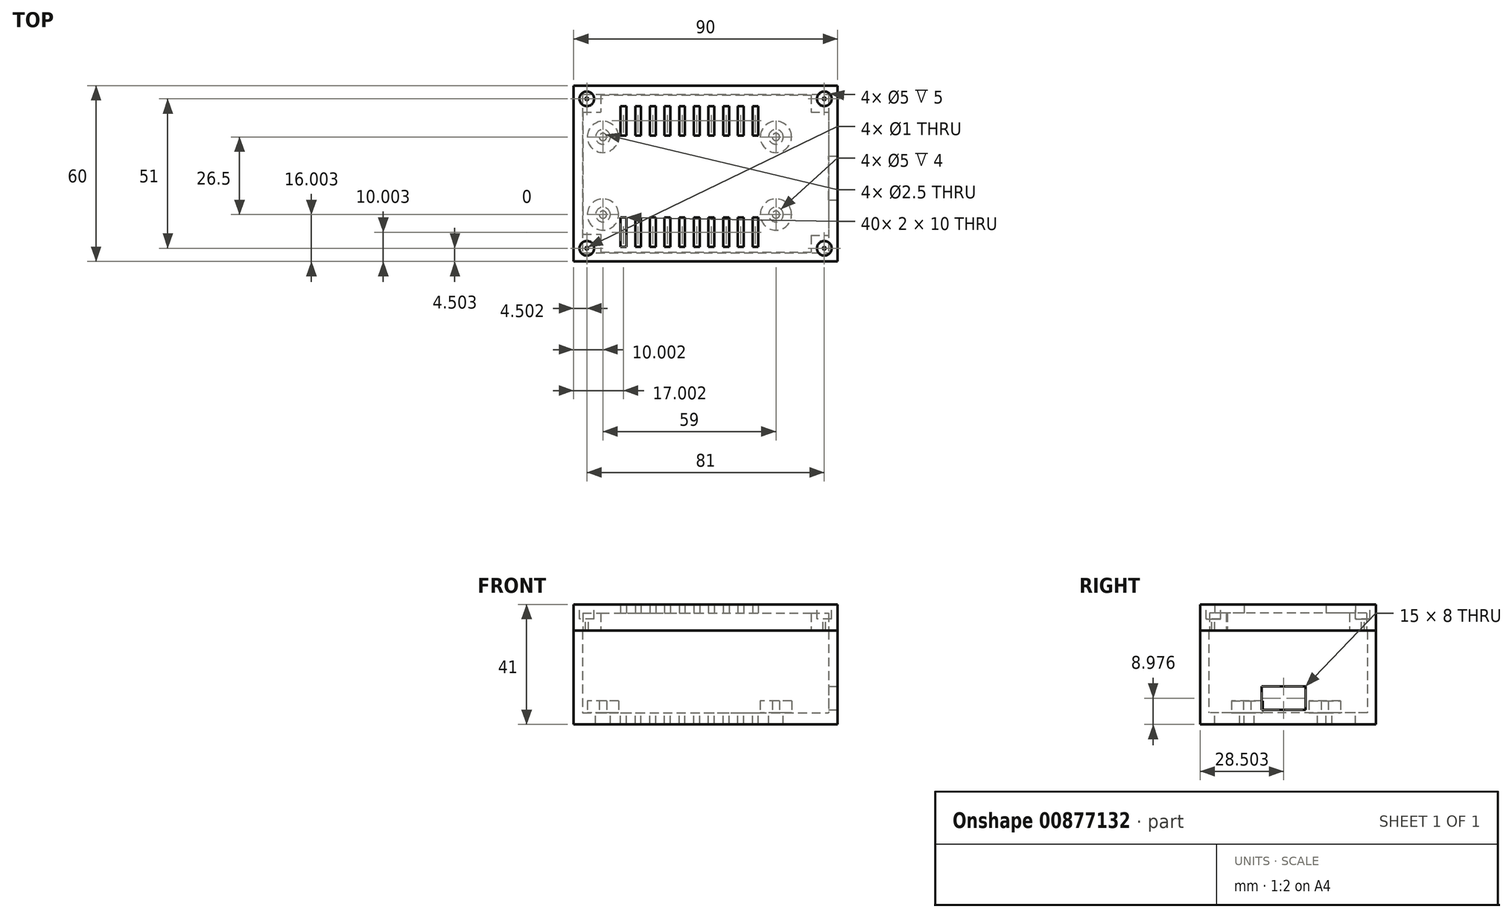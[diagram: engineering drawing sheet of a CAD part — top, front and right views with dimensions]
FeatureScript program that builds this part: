
annotation { "Feature Type Name" : "Feature", "Feature Type Description" : "" }
export const myFeature = defineFeature(function(context is Context, id is Id, definition is map)
    precondition{}
    {
        {
            var Q0;
            Q0=qCreatedBy(makeId("Top.planeOp"),FACE);
            var sketch = newSketch(context, id + "F0", { "sketchPlane" : qUnion([Q0])});
            skLineSegment(sketch, "E0.bottom", {"start": v(-60.63, 23.74) * mm, "end": v(29.37, 23.74) * mm});
            skLineSegment(sketch, "E0.top", {"start": v(-60.63, -36.26) * mm, "end": v(29.37, -36.26) * mm});
            skLineSegment(sketch, "E0.left", {"start": v(-60.63, 23.74) * mm, "end": v(-60.63, -36.26) * mm});
            skLineSegment(sketch, "E0.right", {"start": v(29.37, 23.74) * mm, "end": v(29.37, -36.26) * mm});
            skSolve(sketch);
        }
        {
            var Q0;
            Q0=makeQuery(id+"F0.imprint","IMPRINT",FACE,{"disambiguationData":[TD([[makeQuery(id+"F0.imprint","IMPRINT",EDGE,{"derivedFrom":sQuery(id+"F0.wireOp",EDGE,"E0.bottom")}),-1.0]])]});
            extrude(context, id + "F1", {"entities" : qUnion([Q0]), "depth" : 4 * mm, "offsetDistance" : 25 * mm});
        }
        {
            var Q0;
            Q0=makeQuery(id+"F1.opExtrude","CAP_FACE",FACE,{"disambiguationData":[OSD([sQuery(id+"F0.wireOp",EDGE,"E0.bottom"),sQuery(id+"F0.wireOp",EDGE,"E0.top"),sQuery(id+"F0.wireOp",EDGE,"E0.left"),sQuery(id+"F0.wireOp",EDGE,"E0.right")])],"isStart":false});
            var sketch = newSketch(context, id + "F2", { "sketchPlane" : qUnion([Q0])});
            skCircle(sketch, "E1", {"center": v(-50.63, 6.24) * mm, "radius": 2.3 * mm});
            skCircle(sketch, "E2", {"center": v(-50.63, -20.26) * mm, "radius": 2.3 * mm});
            skCircle(sketch, "E3", {"center": v(8.37, 6.24) * mm, "radius": 2.3 * mm});
            skCircle(sketch, "E4", {"center": v(8.37, -20.26) * mm, "radius": 2.3 * mm});
            skSolve(sketch);
        }
        {
            var Q0;
            Q0=sQuery(id+"F2.wireOp",VERTEX,"E1.center");
            var Q1;
            Q1=sQuery(id+"F2.wireOp",VERTEX,"E3.center");
            var Q2;
            Q2=sQuery(id+"F2.wireOp",VERTEX,"E4.center");
            var Q3;
            Q3=sQuery(id+"F2.wireOp",VERTEX,"E2.center");
            var Q4;
            Q4=makeQuery(id+"F1.opExtrude","SWEPT_BODY",BODY,{"disambiguationData":[OSD([sQuery(id+"F0.wireOp",EDGE,"E0.bottom"),sQuery(id+"F0.wireOp",EDGE,"E0.top"),sQuery(id+"F0.wireOp",EDGE,"E0.left"),sQuery(id+"F0.wireOp",EDGE,"E0.right")])]});
            hole(context, id + "F3", {"style" : HoleStyle.SIMPLE, "endStyle" : HoleEndStyle.THROUGH, "holeDiameter" : 5 * mm, "majorDiameter" : 5 * mm, "isTappedThrough" : true, "tappedDepth" : 12 * mm, "tapClearance" : 3, "locations" : qUnion([Q0, Q1, Q2, Q3]), "scope" : qUnion([Q4])});
        }
        {
            var Q0;
            Q0=makeQuery(id+"F1.opExtrude","CAP_FACE",FACE,{"disambiguationData":[OSD([sQuery(id+"F0.wireOp",EDGE,"E0.bottom"),sQuery(id+"F0.wireOp",EDGE,"E0.top"),sQuery(id+"F0.wireOp",EDGE,"E0.left"),sQuery(id+"F0.wireOp",EDGE,"E0.right")])],"isStart":false});
            var sketch = newSketch(context, id + "F4", { "sketchPlane" : qUnion([Q0])});
            skCircle(sketch, "E5", {"center": v(-50.63, 6.24) * mm, "radius": 5.34 * mm});
            skCircle(sketch, "E6", {"center": v(-50.63, -20.26) * mm, "radius": 5.34 * mm});
            skCircle(sketch, "E7", {"center": v(8.37, -20.26) * mm, "radius": 5.34 * mm});
            skCircle(sketch, "E8", {"center": v(8.37, 6.24) * mm, "radius": 5.34 * mm});
            skSolve(sketch);
        }
        {
            var Q0;
            Q0 = qSketchRegion(id + "F4", true);
            extrude(context, id + "F5", {"entities" : qUnion([Q0]), "operationType" : NewBodyOperationType.ADD, "depth" : 4 * mm, "offsetDistance" : 25 * mm});
        }
        {
            var Q0;
            Q0=sQuery(id+"F4.wireOp",VERTEX,"E5.center");
            var Q1;
            Q1=sQuery(id+"F4.wireOp",VERTEX,"E8.center");
            var Q2;
            Q2=sQuery(id+"F4.wireOp",VERTEX,"E7.center");
            var Q3;
            Q3=sQuery(id+"F4.wireOp",VERTEX,"E6.center");
            var Q4;
            Q4=makeQuery(id+"F1.opExtrude","SWEPT_BODY",BODY,{"disambiguationData":[OSD([sQuery(id+"F0.wireOp",EDGE,"E0.bottom"),sQuery(id+"F0.wireOp",EDGE,"E0.top"),sQuery(id+"F0.wireOp",EDGE,"E0.left"),sQuery(id+"F0.wireOp",EDGE,"E0.right")])]});
            hole(context, id + "F6", {"style" : HoleStyle.SIMPLE, "endStyle" : HoleEndStyle.THROUGH, "oppositeDirection" : true, "holeDiameter" : 2.5 * mm, "majorDiameter" : 5 * mm, "isTappedThrough" : true, "tappedDepth" : 12 * mm, "tapClearance" : 3, "locations" : qUnion([Q0, Q1, Q2, Q3]), "scope" : qUnion([Q4])});
        }
        {
            var Q0;
            Q0=makeQuery(id+"F4.imprint","IMPRINT",FACE,{"disambiguationData":[TD([[makeQuery(id+"F4.imprint","IMPRINT",EDGE,{"derivedFrom":sQuery(id+"F4.wireOp",EDGE,"E5")}),-1.0]])]});
            var sketch = newSketch(context, id + "F7", { "sketchPlane" : qUnion([Q0])});
            skLineSegment(sketch, "E9.bottom", {"start": v(-44.63, -21.26) * mm, "end": v(-42.63, -21.26) * mm});
            skLineSegment(sketch, "E9.top", {"start": v(-44.63, -31.26) * mm, "end": v(-42.63, -31.26) * mm});
            skLineSegment(sketch, "E9.left", {"start": v(-44.63, -21.26) * mm, "end": v(-44.63, -31.26) * mm});
            skLineSegment(sketch, "E9.right", {"start": v(-42.63, -21.26) * mm, "end": v(-42.63, -31.26) * mm});
            skLineSegment(sketch, "E10.1.0.0", {"start": v(-39.63, -21.26) * mm, "end": v(-39.63, -31.26) * mm});
            skLineSegment(sketch, "E10.1.0.1", {"start": v(-39.63, -21.26) * mm, "end": v(-37.63, -21.26) * mm});
            skLineSegment(sketch, "E10.1.0.2", {"start": v(-37.63, -21.26) * mm, "end": v(-37.63, -31.26) * mm});
            skLineSegment(sketch, "E10.1.0.3", {"start": v(-39.63, -31.26) * mm, "end": v(-37.63, -31.26) * mm});
            skLineSegment(sketch, "E10.2.0.0", {"start": v(-34.63, -21.26) * mm, "end": v(-34.63, -31.26) * mm});
            skLineSegment(sketch, "E10.2.0.1", {"start": v(-34.63, -21.26) * mm, "end": v(-32.63, -21.26) * mm});
            skLineSegment(sketch, "E10.2.0.2", {"start": v(-32.63, -21.26) * mm, "end": v(-32.63, -31.26) * mm});
            skLineSegment(sketch, "E10.2.0.3", {"start": v(-34.63, -31.26) * mm, "end": v(-32.63, -31.26) * mm});
            skLineSegment(sketch, "E10.direction1", {"start": v(-44.63, -31.26) * mm, "end": v(-39.63, -31.26) * mm, "construction": true});
            skLineSegment(sketch, "E11.0.3.0", {"start": v(-29.63, -21.26) * mm, "end": v(-29.63, -31.26) * mm});
            skLineSegment(sketch, "E11.3.3.0", {"start": v(-29.63, -21.26) * mm, "end": v(-27.63, -21.26) * mm});
            skLineSegment(sketch, "E11.6.3.0", {"start": v(-27.63, -21.26) * mm, "end": v(-27.63, -31.26) * mm});
            skLineSegment(sketch, "E11.9.3.0", {"start": v(-29.63, -31.26) * mm, "end": v(-27.63, -31.26) * mm});
            skLineSegment(sketch, "E11.0.4.0", {"start": v(-24.63, -21.26) * mm, "end": v(-24.63, -31.26) * mm});
            skLineSegment(sketch, "E11.3.4.0", {"start": v(-24.63, -21.26) * mm, "end": v(-22.63, -21.26) * mm});
            skLineSegment(sketch, "E11.6.4.0", {"start": v(-22.63, -21.26) * mm, "end": v(-22.63, -31.26) * mm});
            skLineSegment(sketch, "E11.9.4.0", {"start": v(-24.63, -31.26) * mm, "end": v(-22.63, -31.26) * mm});
            skLineSegment(sketch, "E11.0.5.0", {"start": v(-19.63, -21.26) * mm, "end": v(-19.63, -31.26) * mm});
            skLineSegment(sketch, "E11.3.5.0", {"start": v(-19.63, -21.26) * mm, "end": v(-17.63, -21.26) * mm});
            skLineSegment(sketch, "E11.6.5.0", {"start": v(-17.63, -21.26) * mm, "end": v(-17.63, -31.26) * mm});
            skLineSegment(sketch, "E11.9.5.0", {"start": v(-19.63, -31.26) * mm, "end": v(-17.63, -31.26) * mm});
            skLineSegment(sketch, "E11.0.6.0", {"start": v(-14.63, -21.26) * mm, "end": v(-14.63, -31.26) * mm});
            skLineSegment(sketch, "E11.3.6.0", {"start": v(-14.63, -21.26) * mm, "end": v(-12.63, -21.26) * mm});
            skLineSegment(sketch, "E11.6.6.0", {"start": v(-12.63, -21.26) * mm, "end": v(-12.63, -31.26) * mm});
            skLineSegment(sketch, "E11.9.6.0", {"start": v(-14.63, -31.26) * mm, "end": v(-12.63, -31.26) * mm});
            skLineSegment(sketch, "E11.0.7.0", {"start": v(-9.63, -21.26) * mm, "end": v(-9.63, -31.26) * mm});
            skLineSegment(sketch, "E11.3.7.0", {"start": v(-9.63, -21.26) * mm, "end": v(-7.63, -21.26) * mm});
            skLineSegment(sketch, "E11.6.7.0", {"start": v(-7.63, -21.26) * mm, "end": v(-7.63, -31.26) * mm});
            skLineSegment(sketch, "E11.9.7.0", {"start": v(-9.63, -31.26) * mm, "end": v(-7.63, -31.26) * mm});
            skLineSegment(sketch, "E11.0.8.0", {"start": v(-4.63, -21.26) * mm, "end": v(-4.63, -31.26) * mm});
            skLineSegment(sketch, "E11.3.8.0", {"start": v(-4.63, -21.26) * mm, "end": v(-2.63, -21.26) * mm});
            skLineSegment(sketch, "E11.6.8.0", {"start": v(-2.63, -21.26) * mm, "end": v(-2.63, -31.26) * mm});
            skLineSegment(sketch, "E11.9.8.0", {"start": v(-4.63, -31.26) * mm, "end": v(-2.63, -31.26) * mm});
            skLineSegment(sketch, "E11.0.9.0", {"start": v(0.37, -21.26) * mm, "end": v(0.37, -31.26) * mm});
            skLineSegment(sketch, "E11.3.9.0", {"start": v(0.37, -21.26) * mm, "end": v(2.37, -21.26) * mm});
            skLineSegment(sketch, "E11.6.9.0", {"start": v(2.37, -21.26) * mm, "end": v(2.37, -31.26) * mm});
            skLineSegment(sketch, "E11.9.9.0", {"start": v(0.37, -31.26) * mm, "end": v(2.37, -31.26) * mm});
            skLineSegment(sketch, "E12.bottom", {"start": v(-44.63, 16.74) * mm, "end": v(-42.63, 16.74) * mm});
            skLineSegment(sketch, "E12.top", {"start": v(-44.63, 6.74) * mm, "end": v(-42.63, 6.74) * mm});
            skLineSegment(sketch, "E12.left", {"start": v(-44.63, 16.74) * mm, "end": v(-44.63, 6.74) * mm});
            skLineSegment(sketch, "E12.right", {"start": v(-42.63, 16.74) * mm, "end": v(-42.63, 6.74) * mm});
            skLineSegment(sketch, "E13.1.0.0", {"start": v(-39.63, 16.74) * mm, "end": v(-39.63, 6.74) * mm});
            skLineSegment(sketch, "E13.1.0.1", {"start": v(-39.63, 16.74) * mm, "end": v(-37.63, 16.74) * mm});
            skLineSegment(sketch, "E13.1.0.2", {"start": v(-37.63, 16.74) * mm, "end": v(-37.63, 6.74) * mm});
            skLineSegment(sketch, "E13.1.0.3", {"start": v(-39.63, 6.74) * mm, "end": v(-37.63, 6.74) * mm});
            skLineSegment(sketch, "E13.2.0.0", {"start": v(-34.63, 16.74) * mm, "end": v(-34.63, 6.74) * mm});
            skLineSegment(sketch, "E13.2.0.1", {"start": v(-34.63, 16.74) * mm, "end": v(-32.63, 16.74) * mm});
            skLineSegment(sketch, "E13.2.0.2", {"start": v(-32.63, 16.74) * mm, "end": v(-32.63, 6.74) * mm});
            skLineSegment(sketch, "E13.2.0.3", {"start": v(-34.63, 6.74) * mm, "end": v(-32.63, 6.74) * mm});
            skLineSegment(sketch, "E13.direction1", {"start": v(-44.63, 6.74) * mm, "end": v(-39.63, 6.74) * mm, "construction": true});
            skLineSegment(sketch, "E14.0.3.0", {"start": v(-29.63, 16.74) * mm, "end": v(-29.63, 6.74) * mm});
            skLineSegment(sketch, "E14.3.3.0", {"start": v(-29.63, 16.74) * mm, "end": v(-27.63, 16.74) * mm});
            skLineSegment(sketch, "E14.6.3.0", {"start": v(-27.63, 16.74) * mm, "end": v(-27.63, 6.74) * mm});
            skLineSegment(sketch, "E14.9.3.0", {"start": v(-29.63, 6.74) * mm, "end": v(-27.63, 6.74) * mm});
            skLineSegment(sketch, "E14.0.4.0", {"start": v(-24.63, 16.74) * mm, "end": v(-24.63, 6.74) * mm});
            skLineSegment(sketch, "E14.3.4.0", {"start": v(-24.63, 16.74) * mm, "end": v(-22.63, 16.74) * mm});
            skLineSegment(sketch, "E14.6.4.0", {"start": v(-22.63, 16.74) * mm, "end": v(-22.63, 6.74) * mm});
            skLineSegment(sketch, "E14.9.4.0", {"start": v(-24.63, 6.74) * mm, "end": v(-22.63, 6.74) * mm});
            skLineSegment(sketch, "E14.0.5.0", {"start": v(-19.63, 16.74) * mm, "end": v(-19.63, 6.74) * mm});
            skLineSegment(sketch, "E14.3.5.0", {"start": v(-19.63, 16.74) * mm, "end": v(-17.63, 16.74) * mm});
            skLineSegment(sketch, "E14.6.5.0", {"start": v(-17.63, 16.74) * mm, "end": v(-17.63, 6.74) * mm});
            skLineSegment(sketch, "E14.9.5.0", {"start": v(-19.63, 6.74) * mm, "end": v(-17.63, 6.74) * mm});
            skLineSegment(sketch, "E14.0.6.0", {"start": v(-14.63, 16.74) * mm, "end": v(-14.63, 6.74) * mm});
            skLineSegment(sketch, "E14.3.6.0", {"start": v(-14.63, 16.74) * mm, "end": v(-12.63, 16.74) * mm});
            skLineSegment(sketch, "E14.6.6.0", {"start": v(-12.63, 16.74) * mm, "end": v(-12.63, 6.74) * mm});
            skLineSegment(sketch, "E14.9.6.0", {"start": v(-14.63, 6.74) * mm, "end": v(-12.63, 6.74) * mm});
            skLineSegment(sketch, "E14.0.7.0", {"start": v(-9.63, 16.74) * mm, "end": v(-9.63, 6.74) * mm});
            skLineSegment(sketch, "E14.3.7.0", {"start": v(-9.63, 16.74) * mm, "end": v(-7.63, 16.74) * mm});
            skLineSegment(sketch, "E14.6.7.0", {"start": v(-7.63, 16.74) * mm, "end": v(-7.63, 6.74) * mm});
            skLineSegment(sketch, "E14.9.7.0", {"start": v(-9.63, 6.74) * mm, "end": v(-7.63, 6.74) * mm});
            skLineSegment(sketch, "E14.0.8.0", {"start": v(-4.63, 16.74) * mm, "end": v(-4.63, 6.74) * mm});
            skLineSegment(sketch, "E14.3.8.0", {"start": v(-4.63, 16.74) * mm, "end": v(-2.63, 16.74) * mm});
            skLineSegment(sketch, "E14.6.8.0", {"start": v(-2.63, 16.74) * mm, "end": v(-2.63, 6.74) * mm});
            skLineSegment(sketch, "E14.9.8.0", {"start": v(-4.63, 6.74) * mm, "end": v(-2.63, 6.74) * mm});
            skLineSegment(sketch, "E14.0.9.0", {"start": v(0.37, 16.74) * mm, "end": v(0.37, 6.74) * mm});
            skLineSegment(sketch, "E14.3.9.0", {"start": v(0.37, 16.74) * mm, "end": v(2.37, 16.74) * mm});
            skLineSegment(sketch, "E14.6.9.0", {"start": v(2.37, 16.74) * mm, "end": v(2.37, 6.74) * mm});
            skLineSegment(sketch, "E14.9.9.0", {"start": v(0.37, 6.74) * mm, "end": v(2.37, 6.74) * mm});
            skSolve(sketch);
        }
        {
            var Q0;
            Q0 = qSketchRegion(id + "F7", true);
            extrude(context, id + "F8", {"entities" : qUnion([Q0]), "operationType" : NewBodyOperationType.REMOVE, "oppositeDirection" : true, "depth" : 5 * mm, "offsetDistance" : 25 * mm});
        }
        {
            var Q0;
            Q0=makeQuery(id+"F1.opExtrude","CAP_FACE",FACE,{"disambiguationData":[OSD([sQuery(id+"F0.wireOp",EDGE,"E0.bottom"),sQuery(id+"F0.wireOp",EDGE,"E0.top"),sQuery(id+"F0.wireOp",EDGE,"E0.left"),sQuery(id+"F0.wireOp",EDGE,"E0.right")])],"isStart":false});
            var sketch = newSketch(context, id + "F9", { "sketchPlane" : qUnion([Q0])});
            skLineSegment(sketch, "E15.bottom", {"start": v(-60.63, 23.74) * mm, "end": v(29.37, 23.74) * mm});
            skLineSegment(sketch, "E15.top", {"start": v(-60.63, -36.26) * mm, "end": v(29.37, -36.26) * mm});
            skLineSegment(sketch, "E15.left", {"start": v(-60.63, 23.74) * mm, "end": v(-60.63, -36.26) * mm});
            skLineSegment(sketch, "E15.right", {"start": v(29.37, 23.74) * mm, "end": v(29.37, -36.26) * mm});
            skLineSegment(sketch, "E16.bottom", {"start": v(-57.63, 20.74) * mm, "end": v(26.37, 20.74) * mm});
            skLineSegment(sketch, "E16.top", {"start": v(-57.63, -33.26) * mm, "end": v(26.37, -33.26) * mm});
            skLineSegment(sketch, "E16.left", {"start": v(-57.63, 20.74) * mm, "end": v(-57.63, -33.26) * mm});
            skLineSegment(sketch, "E16.right", {"start": v(26.37, 20.74) * mm, "end": v(26.37, -33.26) * mm});
            skLineSegment(sketch, "E17.bottom", {"start": v(-57.63, 20.74) * mm, "end": v(-51.63, 20.74) * mm});
            skLineSegment(sketch, "E17.top", {"start": v(-57.63, 14.74) * mm, "end": v(-51.63, 14.74) * mm});
            skLineSegment(sketch, "E17.left", {"start": v(-57.63, 20.74) * mm, "end": v(-57.63, 14.74) * mm});
            skLineSegment(sketch, "E17.right", {"start": v(-51.63, 20.74) * mm, "end": v(-51.63, 14.74) * mm});
            skLineSegment(sketch, "E18.bottom", {"start": v(-57.63, -33.26) * mm, "end": v(-51.63, -33.26) * mm});
            skLineSegment(sketch, "E18.top", {"start": v(-57.63, -27.26) * mm, "end": v(-51.63, -27.26) * mm});
            skLineSegment(sketch, "E18.left", {"start": v(-57.63, -33.26) * mm, "end": v(-57.63, -27.26) * mm});
            skLineSegment(sketch, "E18.right", {"start": v(-51.63, -33.26) * mm, "end": v(-51.63, -27.26) * mm});
            skLineSegment(sketch, "E19.bottom", {"start": v(26.37, -33.26) * mm, "end": v(20.37, -33.26) * mm});
            skLineSegment(sketch, "E19.top", {"start": v(26.37, -27.26) * mm, "end": v(20.37, -27.26) * mm});
            skLineSegment(sketch, "E19.left", {"start": v(26.37, -33.26) * mm, "end": v(26.37, -27.26) * mm});
            skLineSegment(sketch, "E19.right", {"start": v(20.37, -33.26) * mm, "end": v(20.37, -27.26) * mm});
            skLineSegment(sketch, "E20.bottom", {"start": v(26.37, 20.74) * mm, "end": v(20.37, 20.74) * mm});
            skLineSegment(sketch, "E20.top", {"start": v(26.37, 14.74) * mm, "end": v(20.37, 14.74) * mm});
            skLineSegment(sketch, "E20.left", {"start": v(26.37, 20.74) * mm, "end": v(26.37, 14.74) * mm});
            skLineSegment(sketch, "E20.right", {"start": v(20.37, 20.74) * mm, "end": v(20.37, 14.74) * mm});
            skSolve(sketch);
        }
        {
            var Q0;
            Q0 = qSketchRegion(id + "F9", true);
            var Q1;
            Q1=makeQuery(id+"F9.imprint","IMPRINT",FACE,{"disambiguationData":[TD([[makeQuery(id+"F9.imprint","IMPRINT",EDGE,{"derivedFrom":sQuery(id+"F9.wireOp",EDGE,"E17.bottom")}),-1.0]])]});
            var Q2;
            Q2=makeQuery(id+"F9.imprint","IMPRINT",FACE,{"disambiguationData":[TD([[makeQuery(id+"F9.imprint","IMPRINT",EDGE,{"derivedFrom":sQuery(id+"F9.wireOp",EDGE,"E20.bottom")}),1.0]])]});
            var Q3;
            Q3=makeQuery(id+"F9.imprint","IMPRINT",FACE,{"disambiguationData":[TD([[makeQuery(id+"F9.imprint","IMPRINT",EDGE,{"derivedFrom":sQuery(id+"F9.wireOp",EDGE,"E19.bottom")}),-1.0]])]});
            var Q4;
            Q4=makeQuery(id+"F9.imprint","IMPRINT",FACE,{"disambiguationData":[TD([[makeQuery(id+"F9.imprint","IMPRINT",EDGE,{"derivedFrom":sQuery(id+"F9.wireOp",EDGE,"E18.bottom")}),1.0]])]});
            extrude(context, id + "F10", {"entities" : qUnion([Q0, Q1, Q2, Q3, Q4]), "operationType" : NewBodyOperationType.ADD, "depth" : 28 * mm, "offsetDistance" : 25 * mm});
        }
        {
            var Q0;
            Q0=makeQuery(id+"F10.boolean.opBoolean","MERGE",FACE,{"derivedFrom":[makeQuery(id+"F1.opExtrude","SWEPT_FACE",FACE,{"disambiguationData":[OSD([sQuery(id+"F0.wireOp",EDGE,"E0.right")])]}),makeQuery(id+"F10.opExtrude","SWEPT_FACE",FACE,{"disambiguationData":[OSD([sQuery(id+"F9.wireOp",EDGE,"E15.right")])]})]});
            var sketch = newSketch(context, id + "F11", { "sketchPlane" : qUnion([Q0])});
            skLineSegment(sketch, "E21.bottom", {"start": v(-15.26, 12.98) * mm, "end": v(-0.26, 12.98) * mm});
            skLineSegment(sketch, "E21.top", {"start": v(-15.26, 4.98) * mm, "end": v(-0.26, 4.98) * mm});
            skLineSegment(sketch, "E21.left", {"start": v(-15.26, 12.98) * mm, "end": v(-15.26, 4.98) * mm});
            skLineSegment(sketch, "E21.right", {"start": v(-0.26, 12.98) * mm, "end": v(-0.26, 4.98) * mm});
            skSolve(sketch);
        }
        {
            var Q0;
            Q0=makeQuery(id+"F11.imprint","IMPRINT",FACE,{"disambiguationData":[TD([[makeQuery(id+"F11.imprint","IMPRINT",EDGE,{"derivedFrom":sQuery(id+"F11.wireOp",EDGE,"E21.bottom")}),-1.0]])]});
            extrude(context, id + "F12", {"entities" : qUnion([Q0]), "operationType" : NewBodyOperationType.REMOVE, "oppositeDirection" : true, "depth" : 5 * mm, "offsetDistance" : 25 * mm});
        }
        {
            var Q0;
            Q0=makeQuery(id+"F10.opExtrude","CAP_FACE",FACE,{"disambiguationData":[OSD([sQuery(id+"F9.wireOp",EDGE,"E15.bottom"),sQuery(id+"F9.wireOp",EDGE,"E15.top"),sQuery(id+"F9.wireOp",EDGE,"E15.left"),sQuery(id+"F9.wireOp",EDGE,"E15.right"),sQuery(id+"F9.wireOp",EDGE,"E16.bottom"),sQuery(id+"F9.wireOp",EDGE,"E16.top"),sQuery(id+"F9.wireOp",EDGE,"E16.left"),sQuery(id+"F9.wireOp",EDGE,"E16.right"),sQuery(id+"F9.wireOp",EDGE,"E17.top"),sQuery(id+"F9.wireOp",EDGE,"E17.right"),sQuery(id+"F9.wireOp",EDGE,"E18.top"),sQuery(id+"F9.wireOp",EDGE,"E18.right"),sQuery(id+"F9.wireOp",EDGE,"E19.top"),sQuery(id+"F9.wireOp",EDGE,"E19.right"),sQuery(id+"F9.wireOp",EDGE,"E20.top"),sQuery(id+"F9.wireOp",EDGE,"E20.right")])],"isStart":false});
            var sketch = newSketch(context, id + "F13", { "sketchPlane" : qUnion([Q0])});
            skPoint(sketch, "E22", {"position": v(24.87, 19.24) * mm});
            skPoint(sketch, "E23", {"position": v(24.87, -31.76) * mm});
            skPoint(sketch, "E24", {"position": v(-56.13, -31.76) * mm});
            skPoint(sketch, "E25", {"position": v(-56.13, 19.24) * mm});
            skCircle(sketch, "E26", {"center": v(-56.13, 19.24) * mm, "radius": 1 * mm});
            skCircle(sketch, "E27", {"center": v(24.87, 19.24) * mm, "radius": 1 * mm});
            skCircle(sketch, "E28", {"center": v(24.87, -31.76) * mm, "radius": 1 * mm});
            skCircle(sketch, "E29", {"center": v(-56.13, -31.76) * mm, "radius": 1 * mm});
            skSolve(sketch);
        }
        {
            var Q0;
            Q0 = qSketchRegion(id + "F13", true);
            extrude(context, id + "F14", {"entities" : qUnion([Q0]), "operationType" : NewBodyOperationType.REMOVE, "oppositeDirection" : true, "depth" : 10 * mm, "offsetDistance" : 25 * mm});
        }
        {
            var Q0;
            Q0=makeQuery(id+"F10.opExtrude","CAP_FACE",FACE,{"disambiguationData":[OSD([sQuery(id+"F9.wireOp",EDGE,"E15.bottom"),sQuery(id+"F9.wireOp",EDGE,"E15.top"),sQuery(id+"F9.wireOp",EDGE,"E15.left"),sQuery(id+"F9.wireOp",EDGE,"E15.right"),sQuery(id+"F9.wireOp",EDGE,"E16.bottom"),sQuery(id+"F9.wireOp",EDGE,"E16.top"),sQuery(id+"F9.wireOp",EDGE,"E16.left"),sQuery(id+"F9.wireOp",EDGE,"E16.right"),sQuery(id+"F9.wireOp",EDGE,"E17.top"),sQuery(id+"F9.wireOp",EDGE,"E17.right"),sQuery(id+"F9.wireOp",EDGE,"E18.top"),sQuery(id+"F9.wireOp",EDGE,"E18.right"),sQuery(id+"F9.wireOp",EDGE,"E19.top"),sQuery(id+"F9.wireOp",EDGE,"E19.right"),sQuery(id+"F9.wireOp",EDGE,"E20.top"),sQuery(id+"F9.wireOp",EDGE,"E20.right")])],"isStart":false});
            var sketch = newSketch(context, id + "F15", { "sketchPlane" : qUnion([Q0])});
            skLineSegment(sketch, "E30.bottom", {"start": v(-60.63, 23.74) * mm, "end": v(29.37, 23.74) * mm});
            skLineSegment(sketch, "E30.top", {"start": v(-60.63, -36.26) * mm, "end": v(29.37, -36.26) * mm});
            skLineSegment(sketch, "E30.left", {"start": v(-60.63, 23.74) * mm, "end": v(-60.63, -36.26) * mm});
            skLineSegment(sketch, "E30.right", {"start": v(29.37, 23.74) * mm, "end": v(29.37, -36.26) * mm});
            skPoint(sketch, "E31", {"position": v(-56.13, 19.24) * mm});
            skPoint(sketch, "E32", {"position": v(24.87, 19.24) * mm});
            skPoint(sketch, "E33", {"position": v(24.87, -31.76) * mm});
            skPoint(sketch, "E34", {"position": v(-56.13, -31.76) * mm});
            skSolve(sketch);
        }
        {
            var Q0;
            Q0 = qSketchRegion(id + "F15", true);
            extrude(context, id + "F16", {"entities" : qUnion([Q0]), "depth" : 9 * mm, "offsetDistance" : 25 * mm});
        }
        {
            var Q0;
            Q0 = qSketchRegion(id + "F7", true);
            extrude(context, id + "F17", {"entities" : qUnion([Q0]), "operationType" : NewBodyOperationType.REMOVE, "depth" : 40 * mm, "offsetDistance" : 25 * mm});
        }
        {
            var Q0;
            Q0=makeQuery(id+"F15.imprint","IMPRINT",FACE,{"disambiguationData":[TD([[makeQuery(id+"F15.imprint","IMPRINT",EDGE,{"derivedFrom":makeQuery(id+"F10.opExtrude","CAP_EDGE",EDGE,{"disambiguationData":[OSD([sQuery(id+"F9.wireOp",EDGE,"E16.bottom")])],"isStart":false})}),-1.0]])]});
            var sketch = newSketch(context, id + "F18", { "sketchPlane" : qUnion([Q0])});
            skLineSegment(sketch, "E35.bottom", {"start": v(-51.42, 20.52) * mm, "end": v(20.34, 20.52) * mm});
            skLineSegment(sketch, "E35.top", {"start": v(-51.42, -33.09) * mm, "end": v(20.34, -33.09) * mm});
            skLineSegment(sketch, "E35.left", {"start": v(-51.42, 20.52) * mm, "end": v(-51.42, -33.09) * mm});
            skLineSegment(sketch, "E35.right", {"start": v(20.34, 20.52) * mm, "end": v(20.34, -33.09) * mm});
            skLineSegment(sketch, "E36.bottom", {"start": v(-57.53, 14.75) * mm, "end": v(-51.42, 14.75) * mm});
            skLineSegment(sketch, "E36.top", {"start": v(-57.53, -26.98) * mm, "end": v(-51.42, -26.98) * mm});
            skLineSegment(sketch, "E36.left", {"start": v(-57.53, 14.75) * mm, "end": v(-57.53, -26.98) * mm});
            skLineSegment(sketch, "E36.right", {"start": v(-51.42, 14.75) * mm, "end": v(-51.42, -26.98) * mm});
            skLineSegment(sketch, "E37.bottom", {"start": v(20.34, 14.75) * mm, "end": v(26.28, 14.75) * mm});
            skLineSegment(sketch, "E37.top", {"start": v(20.34, -27.33) * mm, "end": v(26.28, -27.33) * mm});
            skLineSegment(sketch, "E37.left", {"start": v(20.34, 14.75) * mm, "end": v(20.34, -27.33) * mm});
            skLineSegment(sketch, "E37.right", {"start": v(26.28, 14.75) * mm, "end": v(26.28, -27.33) * mm});
            skSolve(sketch);
        }
        {
            var Q0;
            Q0 = qSketchRegion(id + "F18", true);
            extrude(context, id + "F19", {"entities" : qUnion([Q0]), "operationType" : NewBodyOperationType.REMOVE, "depth" : 6 * mm, "offsetDistance" : 25 * mm});
        }
        {
            var Q0;
            Q0=makeQuery(id+"F16.opExtrude","CAP_FACE",FACE,{"disambiguationData":[OSD([sQuery(id+"F15.wireOp",EDGE,"E30.bottom"),sQuery(id+"F15.wireOp",EDGE,"E30.top"),sQuery(id+"F15.wireOp",EDGE,"E30.left"),sQuery(id+"F15.wireOp",EDGE,"E30.right")])],"isStart":false});
            var sketch = newSketch(context, id + "F20", { "sketchPlane" : qUnion([Q0])});
            skCircle(sketch, "E38", {"center": v(-56.13, 19.24) * mm, "radius": 2.5 * mm});
            skCircle(sketch, "E39", {"center": v(24.87, 19.24) * mm, "radius": 2.5 * mm});
            skCircle(sketch, "E40", {"center": v(24.87, -31.76) * mm, "radius": 2.5 * mm});
            skCircle(sketch, "E41", {"center": v(-56.13, -31.76) * mm, "radius": 2.5 * mm});
            skSolve(sketch);
        }
        {
            var Q0;
            Q0 = qSketchRegion(id + "F20", true);
            extrude(context, id + "F21", {"entities" : qUnion([Q0]), "operationType" : NewBodyOperationType.REMOVE, "oppositeDirection" : true, "depth" : 5 * mm, "offsetDistance" : 25 * mm});
        }
        {
            var Q0;
            Q0=makeQuery(id+"F16.opExtrude","CAP_FACE",FACE,{"disambiguationData":[OSD([sQuery(id+"F15.wireOp",EDGE,"E30.bottom"),sQuery(id+"F15.wireOp",EDGE,"E30.top"),sQuery(id+"F15.wireOp",EDGE,"E30.left"),sQuery(id+"F15.wireOp",EDGE,"E30.right")])],"isStart":false});
            var sketch = newSketch(context, id + "F22", { "sketchPlane" : qUnion([Q0])});
            skCircle(sketch, "E42", {"center": v(-56.13, 19.24) * mm, "radius": 0.5 * mm});
            skCircle(sketch, "E43", {"center": v(24.87, 19.24) * mm, "radius": 0.5 * mm});
            skCircle(sketch, "E44", {"center": v(24.87, -31.76) * mm, "radius": 0.5 * mm});
            skCircle(sketch, "E45", {"center": v(-56.13, -31.76) * mm, "radius": 0.5 * mm});
            skSolve(sketch);
        }
        {
            var Q0;
            Q0 = qSketchRegion(id + "F22", true);
            extrude(context, id + "F23", {"entities" : qUnion([Q0]), "operationType" : NewBodyOperationType.REMOVE, "oppositeDirection" : true, "depth" : 10 * mm, "offsetDistance" : 25 * mm});
        }
    });
